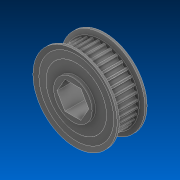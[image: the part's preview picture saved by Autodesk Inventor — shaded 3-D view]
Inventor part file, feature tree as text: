
AUTODESK INVENTOR PART (.ipt)
format: ipt  version: 2022.2 (Build 262287000, 287)  size: 396,800 bytes
history: native  units: in
note: dims shown in document units (in); Inventor stores cm internally (conversion verified against a paired STEP export)
features: revolve x2, other x1
ambient origin geometry x8: Origin, YZ Plane, XZ Plane, XY Plane, X Axis, Y Axis, Z Axis, Center Point
bodies: Solid1 (feature_tree), Solid2 (feature_tree), Solid3 (feature_tree)
feature tree (3):
  revolve  "Revolve1[1]"  [1 undecoded]
  revolve  "Revolve1[2]"  [1 undecoded]
  other  "Cut-Extrude4"
note: 2 required parameter values undecoded (feature->parameter linkage not recoverable at this tier; creation-order binding heuristic only, values carry confidence <= 0.55)
